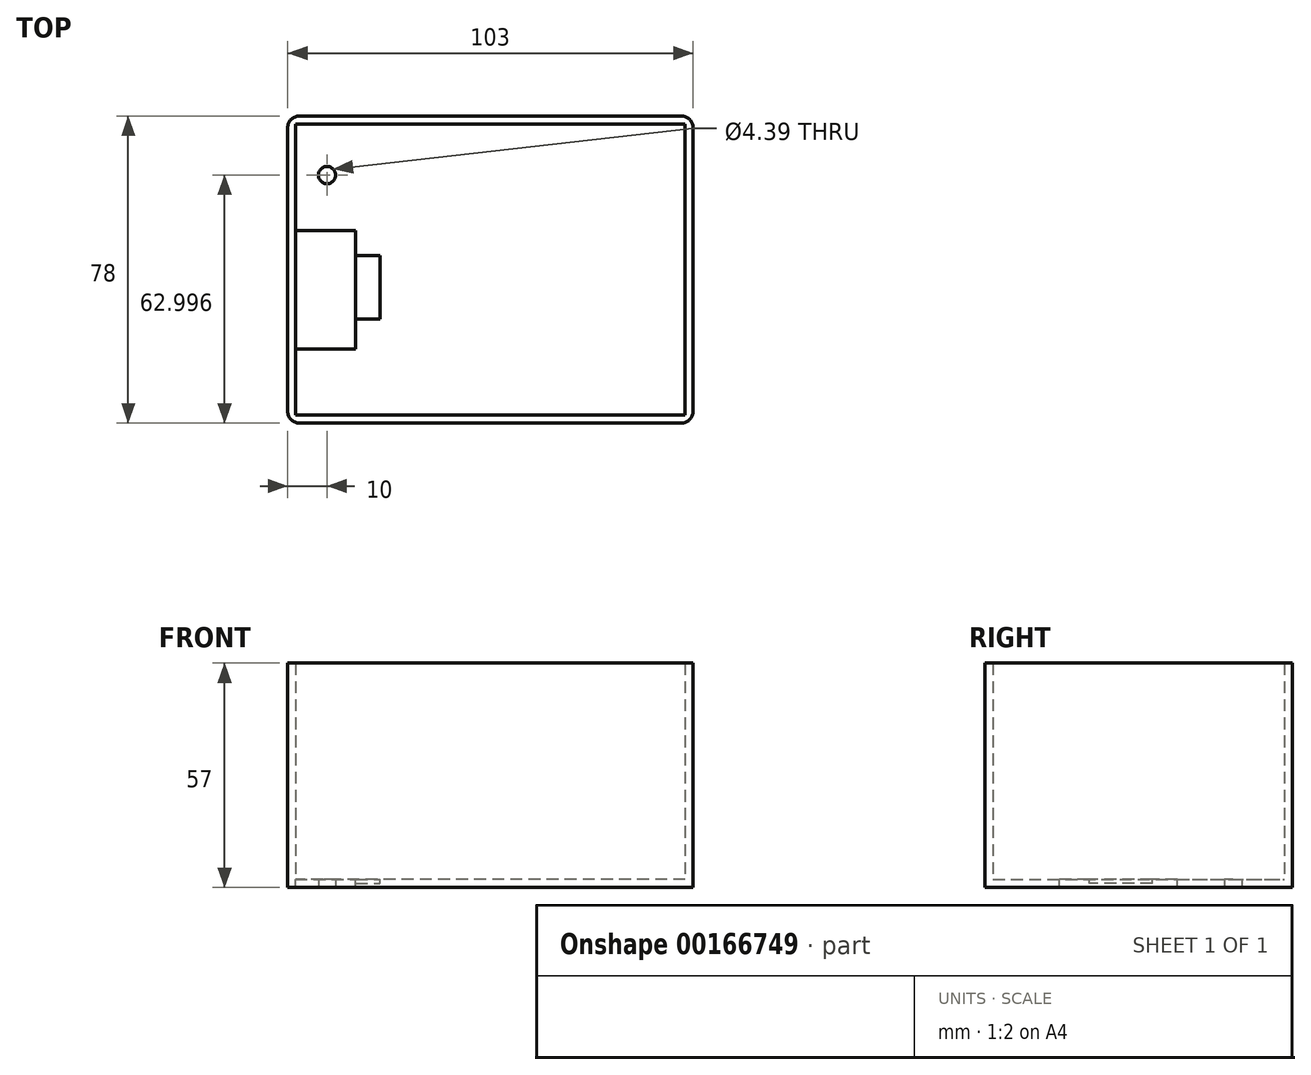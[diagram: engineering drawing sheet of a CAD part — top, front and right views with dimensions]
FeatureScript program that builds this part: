
annotation { "Feature Type Name" : "Feature", "Feature Type Description" : "" }
export const myFeature = defineFeature(function(context is Context, id is Id, definition is map)
    precondition{}
    {
        {
            var Q0;
            Q0=qCreatedBy(makeId("Right.planeOp"),FACE);
            var sketch = newSketch(context, id + "F0", { "sketchPlane" : qUnion([Q0])});
            skLineSegment(sketch, "E0.bottom", {"start": v(-36.62, 26.6) * mm, "end": v(41.38, 26.6) * mm});
            skLineSegment(sketch, "E0.top", {"start": v(-36.62, -30.4) * mm, "end": v(41.38, -30.4) * mm});
            skLineSegment(sketch, "E0.left", {"start": v(-36.62, 26.6) * mm, "end": v(-36.62, -30.4) * mm});
            skLineSegment(sketch, "E0.right", {"start": v(41.38, 26.6) * mm, "end": v(41.38, -30.4) * mm});
            skSolve(sketch);
        }
        {
            var Q0;
            Q0=makeQuery(id+"F0.imprint","IMPRINT",FACE,{"disambiguationData":[TD([[makeQuery(id+"F0.imprint","IMPRINT",EDGE,{"derivedFrom":sQuery(id+"F0.wireOp",EDGE,"E0.bottom")}),-1.0]])]});
            extrude(context, id + "F1", {"entities" : qUnion([Q0]), "depth" : 103 * mm});
        }
        {
            var Q0;
            Q0=makeQuery(id+"F1.opExtrude","SWEPT_FACE",FACE,{"disambiguationData":[OSD([sQuery(id+"F0.wireOp",EDGE,"E0.bottom")])]});
            shell(context, id + "F2", {"entities" : qUnion([Q0]), "thickness" : 2 * mm});
        }
        {
            var Q0;
            Q0=makeQuery(id+"F2.opShell","OFFSET_FACE",FACE,{"disambiguationData":[OSD([sQuery(id+"F0.wireOp",EDGE,"E0.top")])]});
            var sketch = newSketch(context, id + "F3", { "sketchPlane" : qUnion([Q0])});
            skLineSegment(sketch, "E1.bottom", {"start": v(2, 12.24) * mm, "end": v(17.3, 12.24) * mm});
            skLineSegment(sketch, "E1.top", {"start": v(2, -17.76) * mm, "end": v(17.3, -17.76) * mm});
            skLineSegment(sketch, "E1.left", {"start": v(2, 12.24) * mm, "end": v(2, -17.76) * mm});
            skLineSegment(sketch, "E1.right", {"start": v(17.3, 12.24) * mm, "end": v(17.3, -17.76) * mm});
            skSolve(sketch);
        }
        {
            var Q0;
            Q0 = qSketchRegion(id + "F3", true);
            extrude(context, id + "F4", {"entities" : qUnion([Q0]), "operationType" : NewBodyOperationType.REMOVE, "oppositeDirection" : true, "depth" : 2 * mm});
        }
        {
            var Q0;
            Q0=makeQuery(id+"F2.opShell","OFFSET_FACE",FACE,{"disambiguationData":[OSD([sQuery(id+"F0.wireOp",EDGE,"E0.top")])]});
            var sketch = newSketch(context, id + "F5", { "sketchPlane" : qUnion([Q0])});
            skLineSegment(sketch, "E2.bottom", {"start": v(17.3, 5.87) * mm, "end": v(23.45, 5.87) * mm});
            skLineSegment(sketch, "E2.top", {"start": v(17.3, -10.15) * mm, "end": v(23.45, -10.15) * mm});
            skLineSegment(sketch, "E2.left", {"start": v(17.3, 5.87) * mm, "end": v(17.3, -10.15) * mm});
            skLineSegment(sketch, "E2.right", {"start": v(23.45, 5.87) * mm, "end": v(23.45, -10.15) * mm});
            skSolve(sketch);
        }
        {
            var Q0;
            Q0=makeQuery(id+"F5.imprint","IMPRINT",FACE,{"disambiguationData":[TD([[makeQuery(id+"F5.imprint","IMPRINT",EDGE,{"derivedFrom":sQuery(id+"F5.wireOp",EDGE,"E2.bottom")}),-1.0]])]});
            extrude(context, id + "F6", {"entities" : qUnion([Q0]), "operationType" : NewBodyOperationType.REMOVE, "oppositeDirection" : true, "depth" : 1 * mm});
        }
        {
            var Q0;
            Q0=makeQuery(id+"F1.opExtrude","CAP_EDGE",EDGE,{"disambiguationData":[OSD([sQuery(id+"F0.wireOp",EDGE,"E0.left")])],"isStart":true});
            var Q1;
            Q1=makeQuery(id+"F1.opExtrude","CAP_EDGE",EDGE,{"disambiguationData":[OSD([sQuery(id+"F0.wireOp",EDGE,"E0.right")])],"isStart":true});
            var Q2;
            Q2=makeQuery(id+"F1.opExtrude","CAP_EDGE",EDGE,{"disambiguationData":[OSD([sQuery(id+"F0.wireOp",EDGE,"E0.right")])],"isStart":false});
            var Q3;
            Q3=makeQuery(id+"F1.opExtrude","CAP_EDGE",EDGE,{"disambiguationData":[OSD([sQuery(id+"F0.wireOp",EDGE,"E0.left")])],"isStart":false});
            fillet(context, id + "F7", {"entities" : qUnion([Q0, Q1, Q2, Q3]), "radius" : 3 * mm, "tangentPropagation" : true, "allowEdgeOverflow" : false});
        }
        {
            var Q0;
            Q0=makeQuery(id+"F1.opExtrude","SWEPT_FACE",FACE,{"disambiguationData":[OSD([sQuery(id+"F0.wireOp",EDGE,"E0.top")])]});
            var sketch = newSketch(context, id + "F8", { "sketchPlane" : qUnion([Q0])});
            skCircle(sketch, "E3", {"center": v(10, -26.38) * mm, "radius": 2.2 * mm});
            skSolve(sketch);
        }
        {
            var Q0;
            Q0=makeQuery(id+"F8.imprint","IMPRINT",FACE,{"disambiguationData":[TD([[makeQuery(id+"F8.imprint","IMPRINT",EDGE,{"derivedFrom":sQuery(id+"F8.wireOp",EDGE,"E3")}),1.0]])]});
            var Q1;
            Q1=sQuery(id+"F8.wireOp",EDGE,"E3");
            extrude(context, id + "F9", {"entities" : qUnion([Q0]), "operationType" : NewBodyOperationType.REMOVE, "surfaceEntities" : qUnion([Q1]), "oppositeDirection" : true, "depth" : 25 * mm});
        }
    });
